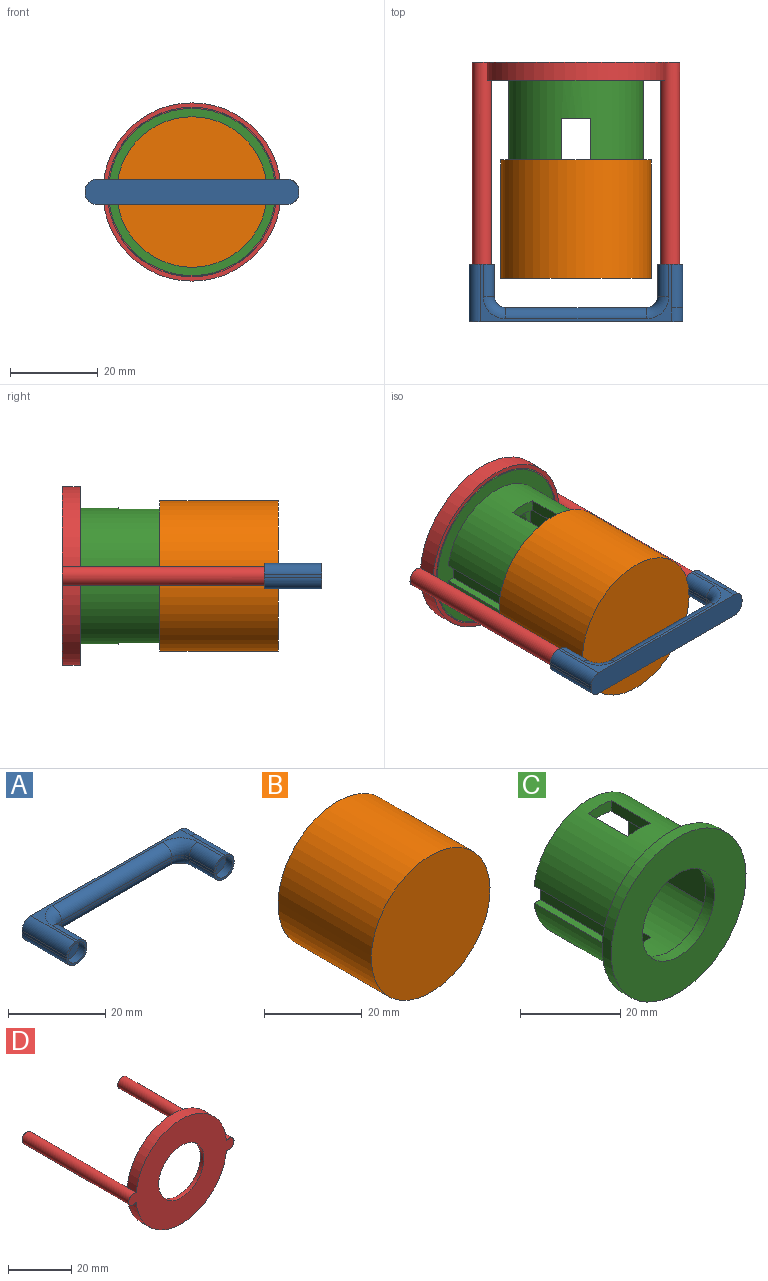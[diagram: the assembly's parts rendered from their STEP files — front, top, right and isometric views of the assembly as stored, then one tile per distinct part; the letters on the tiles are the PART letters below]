
ASSEMBLY  parts=4 mates=3
PART A: 33 faces, bbox 48.7x14.8x5.8 mm
  f0: plane 7.37x0.69mm, normal (1,0,0), area 5.1mm2, adj f14,f18,f20,f32
  f1: plane 43.61x13.08mm, normal (0,0,1), area 55.1mm2, adj f8,f11,f15,f17,f19,f20,f23,f24
  f2: plane 13.08x0.69mm, normal (-1,0,0), area 9mm2, adj f8,f25,f26,f32
  f3: plane 43.61x13.08mm, normal (0,0,-1), area 55.1mm2, adj f8,f9,f10,f13,f14,f16,f21,f22
  f4: plane 7.37x0.69mm, normal (-1,0,0), area 5.1mm2, adj f9,f11,f12,f29
  f5: plane 9.91x0.7mm, normal (1,0,0), area 6.8mm2, adj f7,f21,f23,f29
  f6: plane 32.13x0.69mm, normal (0,-1,0), area 22.2mm2, adj f12,f13,f17,f18
  f7: plane 3.18x0.7mm, normal (1,0,0), area 2.2mm2, adj f5,f8,f22,f24
  f8: plane 48.68x5.77mm, normal (0,1,0), area 275.4mm2, adj f1,f2,f3,f7,f22,f24,f25,f26
  f9: cylinder r=2.54mm len=7.37mm, axis (0,1,0), area 29.4mm2, adj f3,f4,f10,f29
  f10: torus R=5.08mm, axis (0,0,-1), area 21.7mm2, adj f3,f9,f12,f13
  f11: cylinder r=2.54mm len=7.37mm, axis (0,-1,0), area 29.4mm2, adj f1,f4,f15,f29
  f12: cylinder r=2.54mm len=2.54mm, axis (0,0,-1), area 2.8mm2, adj f4,f6,f10,f15
  f13: cylinder r=2.54mm len=32.13mm, axis (-1,0,0), area 128.2mm2, adj f3,f6,f10,f16
  f14: cylinder r=2.54mm len=7.37mm, axis (0,-1,0), area 29.4mm2, adj f0,f3,f16,f32
  f15: torus R=5.08mm, axis (0,0,-1), area 21.7mm2, adj f1,f11,f12,f17
  f16: torus R=5.08mm, axis (0,0,-1), area 21.7mm2, adj f3,f13,f14,f18
  f17: cylinder r=2.54mm len=32.13mm, axis (1,0,0), area 128.2mm2, adj f1,f6,f15,f19
  f18: cylinder r=2.54mm len=2.54mm, axis (0,0,1), area 2.8mm2, adj f0,f6,f16,f19
  f19: torus R=5.08mm, axis (0,0,-1), area 21.7mm2, adj f1,f17,f18,f20
  f20: cylinder r=2.54mm len=7.37mm, axis (0,1,0), area 29.4mm2, adj f0,f1,f19,f32
  f21: cylinder r=2.54mm len=9.91mm, axis (0,-1,0), area 39.5mm2, adj f3,f5,f22,f29
  f22: cylinder r=2.54mm len=3.18mm, axis (0,-1,0), area 12.7mm2, adj f3,f7,f8,f21
  f23: cylinder r=2.54mm len=9.91mm, axis (0,1,0), area 39.5mm2, adj f1,f5,f24,f29
  f24: cylinder r=2.54mm len=3.18mm, axis (0,1,0), area 12.7mm2, adj f1,f7,f8,f23
  f25: cylinder r=2.54mm len=13.08mm, axis (0,-1,0), area 52.2mm2, adj f1,f2,f8,f32
  f26: cylinder r=2.54mm len=13.08mm, axis (0,1,0), area 52.2mm2, adj f2,f3,f8,f32
  f27: plane 4.85x4.85mm, normal (0,-1,0), area 18.5mm2, adj f28
  f28: cylinder r=2.43mm len=4.85mm, axis (0,1,0), area 29mm2, adj f27,f29
  f29: plane 5.77x5.74mm, normal (0,-1,0), area 9.1mm2, adj f1,f3,f4,f5,f9,f11,f21,f23
  f30: plane 4.85x4.85mm, normal (0,-1,0), area 18.5mm2, adj f31
  f31: cylinder r=2.43mm len=4.85mm, axis (0,1,0), area 29mm2, adj f30,f32
  f32: plane 5.77x5.74mm, normal (0,-1,0), area 9.1mm2, adj f0,f1,f2,f3,f14,f20,f25,f26
PART B: 12 faces, bbox 34.3x27x34.3 mm
  f0: plane 23.81x1.3mm, normal (0,0,1), area 31mm2, adj f1,f7,f9,f11
  f1: cylinder r=16.19mm len=32.23mm, axis (0,1,0), area 1135.6mm2, adj f0,f2,f9,f11
  f2: plane 23.81x1.3mm, normal (0,0,1), area 31mm2, adj f1,f3,f9,f11
  f3: plane 23.81x3.18mm, normal (-1,0,0), area 75.6mm2, adj f2,f4,f9,f11
  f4: plane 23.81x1.3mm, normal (0,0,-1), area 31mm2, adj f3,f5,f9,f11
  f5: cylinder r=16.19mm len=32.23mm, axis (0,1,0), area 1135.6mm2, adj f4,f6,f9,f11
  f6: plane 23.81x1.3mm, normal (0,0,-1), area 31mm2, adj f5,f7,f9,f11
  f7: plane 23.81x3.18mm, normal (1,0,0), area 75.6mm2, adj f0,f6,f9,f11
  f8: cylinder r=17.14mm len=34.29mm, axis (0,1,0), area 2907.2mm2, adj f9,f10
  f9: plane 34.29x34.29mm, normal (0,1,0), area 108.4mm2, adj f0,f1,f2,f3,f4,f5,f6,f7
  f10: plane 34.29x34.29mm, normal (0,-1,0), area 923.5mm2, adj f8
  f11: plane 32.39x32.23mm, normal (0,1,0), area 815.1mm2, adj f0,f1,f2,f3,f4,f5,f6,f7
PART C: 30 faces, bbox 38.1x25.4x38.1 mm
  f0: cylinder r=15.56mm len=30.83mm, axis (0,1,0), area 948.9mm2, adj f4,f5,f10,f22,f23,f24,f25,f26
  f1: cylinder r=15.56mm len=30.83mm, axis (0,1,0), area 948.9mm2, adj f2,f3,f10,f18,f19,f20,f21,f26
  f2: plane 22.86x1.75mm, normal (0,0,-1), area 39.9mm2, adj f1,f6,f10,f26
  f3: plane 22.86x1.75mm, normal (0,0,-1), area 39.9mm2, adj f1,f7,f10,f26
  f4: plane 22.86x1.75mm, normal (0,0,1), area 39.9mm2, adj f0,f7,f10,f26
  f5: plane 22.86x1.75mm, normal (0,0,1), area 39.9mm2, adj f0,f6,f10,f26
  f6: plane 22.86x4.19mm, normal (-1,0,0), area 95.8mm2, adj f2,f5,f10,f26
  f7: plane 22.86x4.19mm, normal (1,0,0), area 95.8mm2, adj f3,f4,f10,f26
  f8: cylinder r=13.02mm len=24.33mm, axis (0,1,0), area 645.7mm2, adj f10,f13,f14,f17,f22,f23,f24,f25
  f9: cylinder r=13.02mm len=24.33mm, axis (0,1,0), area 645.7mm2, adj f10,f11,f12,f17,f18,f19,f20,f21
  f10: plane 31.12x30.83mm, normal (0,1,0), area 242.4mm2, adj f0,f1,f2,f3,f4,f5,f6,f7
  f11: plane 22.86x1.04mm, normal (0,0,1), area 23.7mm2, adj f9,f10,f15,f17
  f12: plane 22.86x1.04mm, normal (0,0,1), area 23.7mm2, adj f9,f10,f16,f17
  f13: plane 22.86x1.04mm, normal (0,0,-1), area 23.7mm2, adj f8,f10,f16,f17
  f14: plane 22.86x1.04mm, normal (0,0,-1), area 23.7mm2, adj f8,f10,f15,f17
  f15: plane 22.86x9.27mm, normal (1,0,0), area 211.9mm2, adj f10,f11,f14,f17
  f16: plane 22.86x9.27mm, normal (-1,0,0), area 211.9mm2, adj f10,f12,f13,f17
  f17: plane 26.04x24.33mm, normal (0,1,0), area 178.2mm2, adj f8,f9,f11,f12,f13,f14,f15,f16
  f18: plane 11.12x2.61mm, normal (1,0,0), area 29mm2, adj f1,f9,f19,f21
  f19: plane 6.45x2.95mm, normal (0,-1,0), area 16.5mm2, adj f1,f9,f18,f20
  f20: plane 11.12x2.61mm, normal (-1,0,0), area 29mm2, adj f1,f9,f19,f21
  f21: plane 6.45x2.95mm, normal (0,1,0), area 16.5mm2, adj f1,f9,f18,f20
  f22: plane 6.45x2.95mm, normal (0,1,0), area 16.5mm2, adj f0,f8,f23,f25
  f23: plane 11.12x2.61mm, normal (-1,0,0), area 29mm2, adj f0,f8,f22,f24
  f24: plane 6.45x2.95mm, normal (0,-1,0), area 16.5mm2, adj f0,f8,f23,f25
  f25: plane 11.12x2.61mm, normal (1,0,0), area 29mm2, adj f0,f8,f22,f24
  f26: plane 38.1x38.1mm, normal (0,1,0), area 395.2mm2, adj f0,f1,f2,f3,f4,f5,f6,f7
  f27: cylinder r=19.05mm len=38.1mm, axis (0,-1,0), area 304mm2, adj f26,f28
  f28: plane 38.1x38.1mm, normal (0,-1,0), area 815.8mm2, adj f27,f29
  f29: cylinder r=10.16mm len=20.32mm, axis (0,1,0), area 162.1mm2, adj f17,f28
PART D: 12 faces, bbox 47.3x47.9x40.6 mm
  f0: cylinder r=20.32mm len=40.48mm, axis (0,1,0), area 245.7mm2, adj f2,f5,f8,f10
  f1: cylinder r=20.32mm len=40.48mm, axis (0,1,0), area 245.7mm2, adj f5,f7,f8,f10
  f2: plane 40.48x20.32mm, normal (0,1,0), area 60.7mm2, adj f0,f6,f8,f10
  f3: plane 38.61x38.61mm, normal (0,1,0), area 846.4mm2, adj f4,f6
  f4: cylinder r=10.16mm len=20.32mm, axis (0,1,0), area 101.3mm2, adj f3,f5
  f5: plane 47.28x40.64mm, normal (0,-1,0), area 997.3mm2, adj f0,f1,f4,f8,f10
  f6: cylinder r=19.3mm len=38.61mm, axis (0,-1,0), area 301.9mm2, adj f2,f3,f7
  f7: plane 40.48x20.32mm, normal (0,1,0), area 60.7mm2, adj f1,f6,f8,f10
  f8: cylinder r=2.17mm len=47.9mm, axis (0,-1,0), area 635.3mm2, adj f0,f1,f2,f5,f7,f9
  f9: plane 4.34x4.34mm, normal (0,1,0), area 14.8mm2, adj f8
  f10: cylinder r=2.17mm len=47.9mm, axis (0,-1,0), area 635.3mm2, adj f0,f1,f2,f5,f7,f11
  f11: plane 4.34x4.34mm, normal (0,1,0), area 14.8mm2, adj f10
PLACE A rot(axis=(-1,0,0),180deg) t=(0,-45.05,0)mm
PLACE B rot(axis=(0,1,0),180deg) t=(0,-18.1,0)mm
PLACE C rot(axis=(1,0,0),180deg) t=(0,-21.27,0)mm
PLACE D rot(axis=(1,0,0),180deg) t=(0,-21.27,0)mm
MATE slider B.f1 <-> C.f0  axis (0,1,0) through (0,-41.91,0)mm
MATE fastened C.f29 <-> D.f6  axis (0,1,0) through (0,2.54,0)mm
MATE fastened A.f28 <-> D.f10  axis (0,1,0) through (21.47,-43.78,0)mm
